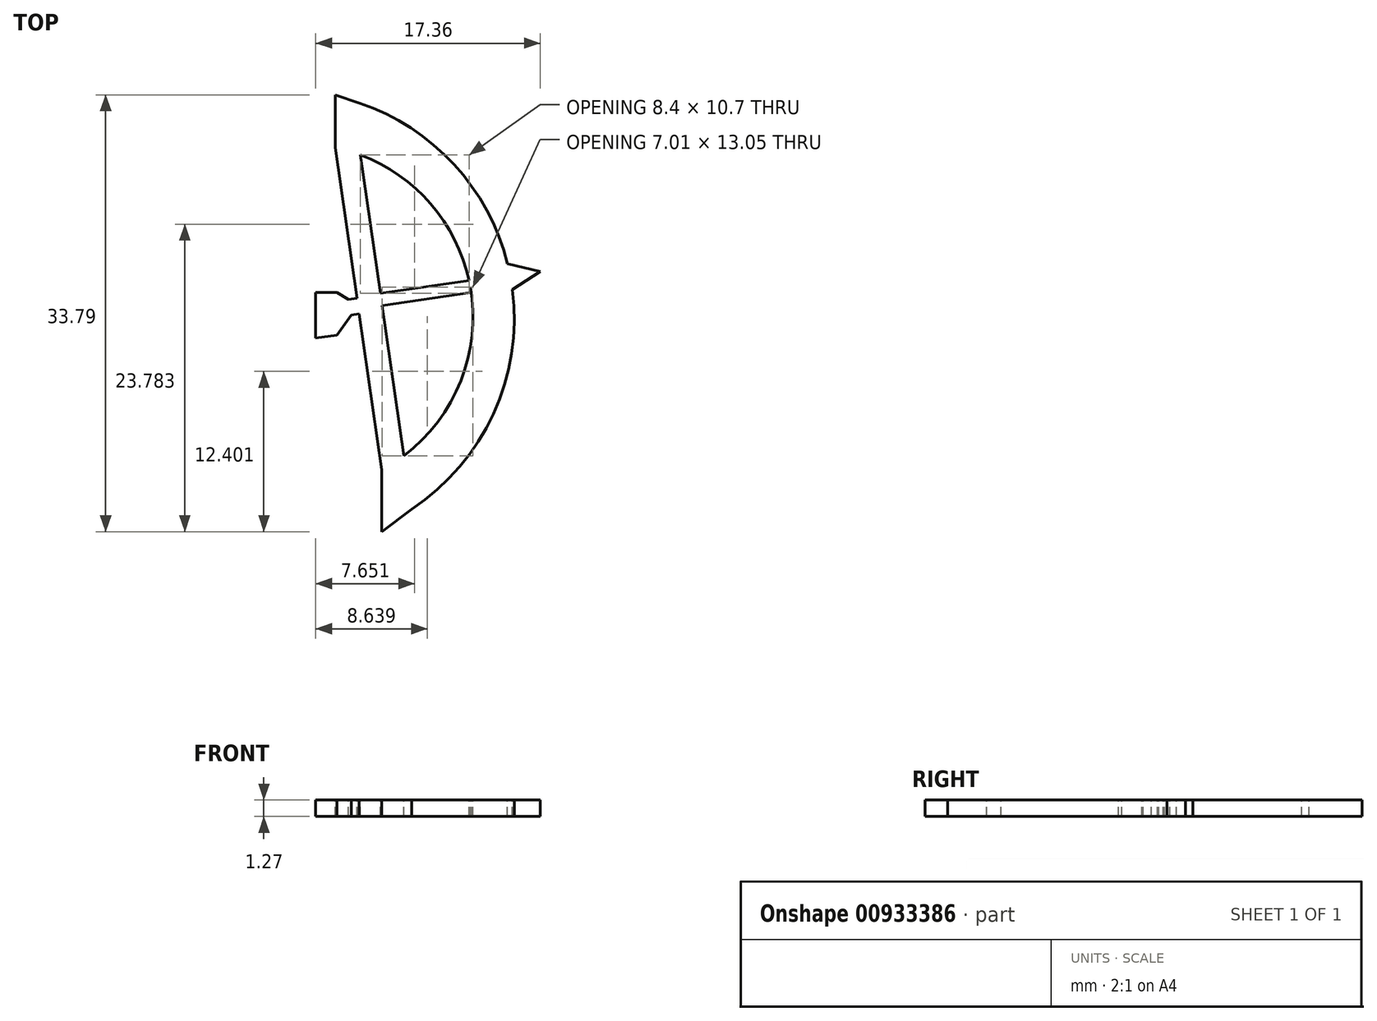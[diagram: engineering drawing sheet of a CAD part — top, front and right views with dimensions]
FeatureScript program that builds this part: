
annotation { "Feature Type Name" : "Feature", "Feature Type Description" : "" }
export const myFeature = defineFeature(function(context is Context, id is Id, definition is map)
    precondition{}
    {
        {
            var Q0;
            Q0=qCreatedBy(makeId("Top.planeOp"),FACE);
            var sketch = newSketch(context, id + "F0", { "sketchPlane" : qUnion([Q0])});
            skArc(sketch, "E0", {"start": v(-42.35, 8.79) * mm, "mid": v(-34.55, 25.75) * mm, "end": v(-46.38, 40.19) * mm});
            skArc(sketch, "E1", {"start": v(-44.65, 11.81) * mm, "mid": v(-37.73, 25.53) * mm, "end": v(-48.25, 36.73) * mm});
            skLineSegment(sketch, "E2", {"start": v(-46.38, 40.19) * mm, "end": v(-48.25, 36.73) * mm});
            skLineSegment(sketch, "E3", {"start": v(-44.65, 11.81) * mm, "end": v(-42.35, 8.79) * mm});
            skLineSegment(sketch, "E4", {"start": v(-46.38, 40.19) * mm, "end": v(-48.25, 40.82) * mm});
            skLineSegment(sketch, "E5", {"start": v(-48.25, 40.82) * mm, "end": v(-48.25, 36.73) * mm});
            skLineSegment(sketch, "E6", {"start": v(-42.35, 8.79) * mm, "end": v(-44.65, 7.03) * mm});
            skLineSegment(sketch, "E7", {"start": v(-44.65, 7.03) * mm, "end": v(-44.65, 11.81) * mm});
            skLineSegment(sketch, "E8", {"start": v(-48.25, 36.73) * mm, "end": v(-44.65, 11.81) * mm});
            skLineSegment(sketch, "E9", {"start": v(-46.38, 36.73) * mm, "end": v(-42.94, 12.9) * mm});
            skLineSegment(sketch, "E10", {"start": v(-37.73, 25.53) * mm, "end": v(-44.62, 24.53) * mm});
            skLineSegment(sketch, "E11", {"start": v(-44.62, 24.53) * mm, "end": v(-46.49, 24.53) * mm});
            skLineSegment(sketch, "E12", {"start": v(-46.49, 24.53) * mm, "end": v(-48.11, 25.55) * mm});
            skLineSegment(sketch, "E13", {"start": v(-48.11, 25.55) * mm, "end": v(-49.75, 25.55) * mm});
            skLineSegment(sketch, "E14", {"start": v(-49.75, 25.55) * mm, "end": v(-49.75, 23.61) * mm});
            skLineSegment(sketch, "E15", {"start": v(-49.75, 23.61) * mm, "end": v(-49.75, 22) * mm});
            skLineSegment(sketch, "E16", {"start": v(-49.75, 22) * mm, "end": v(-48.11, 22.23) * mm});
            skLineSegment(sketch, "E17", {"start": v(-48.11, 22.23) * mm, "end": v(-46.49, 24.53) * mm});
            skLineSegment(sketch, "E18", {"start": v(-47.01, 23.79) * mm, "end": v(-46.4, 23.88) * mm});
            skLineSegment(sketch, "E19", {"start": v(-46.4, 23.88) * mm, "end": v(-46.57, 25.1) * mm});
            skLineSegment(sketch, "E20", {"start": v(-46.57, 25.1) * mm, "end": v(-47.23, 25) * mm});
            skLineSegment(sketch, "E21", {"start": v(-34.92, 27.75) * mm, "end": v(-32.39, 27.17) * mm});
            skLineSegment(sketch, "E22", {"start": v(-32.39, 27.17) * mm, "end": v(-34.55, 25.75) * mm});
            skLineSegment(sketch, "E23", {"start": v(-44.55, 24.1) * mm, "end": v(-37.68, 25.1) * mm});
            skLineSegment(sketch, "E24", {"start": v(-37.68, 25.1) * mm, "end": v(-37.8, 25.95) * mm});
            skLineSegment(sketch, "E25", {"start": v(-37.8, 25.95) * mm, "end": v(-44.68, 24.96) * mm});
            skLineSegment(sketch, "E26", {"start": v(-44.75, 25.47) * mm, "end": v(-37.9, 26.46) * mm});
            skSolve(sketch);
        }
        {
            var Q0;
            {var subQ7=sQuery(id+"F0.wireOp",EDGE,"E2");Q0=makeQuery(id+"F0.imprint","IMPRINT",FACE,{"disambiguationData":[TD([[makeQuery(id+"F0.imprint","IMPRINT",EDGE,{"derivedFrom":subQ7}),1.0]])]});}
            var Q1;
            {var subQ7=sQuery(id+"F0.wireOp",EDGE,"E11");Q1=makeQuery(id+"F0.imprint","IMPRINT",FACE,{"disambiguationData":[TD([[makeQuery(id+"F0.imprint","IMPRINT",EDGE,{"derivedFrom":subQ7}),1.0]])]});}
            var Q2;
            {var subQ4=sQuery(id+"F0.wireOp",EDGE,"E11");Q2=makeQuery(id+"F0.imprint","IMPRINT",FACE,{"disambiguationData":[TD([[makeQuery(id+"F0.imprint","IMPRINT",EDGE,{"derivedFrom":subQ4}),-1.0]])]});}
            var Q3;
            {var subQ0=sQuery(id+"F0.wireOp",EDGE,"E13");Q3=makeQuery(id+"F0.imprint","IMPRINT",FACE,{"disambiguationData":[TD([[makeQuery(id+"F0.imprint","IMPRINT",EDGE,{"derivedFrom":subQ0}),1.0]])]});}
            var Q4;
            {var subQ2=sQuery(id+"F0.wireOp",EDGE,"E21");Q4=makeQuery(id+"F0.imprint","IMPRINT",FACE,{"disambiguationData":[TD([[makeQuery(id+"F0.imprint","IMPRINT",EDGE,{"derivedFrom":subQ2}),-1.0]])]});}
            var Q5;
            Q5=makeQuery(id+"F0.imprint","IMPRINT",FACE,{"disambiguationData":[TD([[makeQuery(id+"F0.imprint","IMPRINT",EDGE,{"derivedFrom":sQuery(id+"F0.wireOp",EDGE,"E3")}),-1.0]])]});
            var Q6;
            Q6=makeQuery(id+"F0.imprint","IMPRINT",FACE,{"disambiguationData":[TD([[makeQuery(id+"F0.imprint","IMPRINT",EDGE,{"derivedFrom":sQuery(id+"F0.wireOp",EDGE,"E2")}),-1.0]])]});
            var Q7;
            {var subQ0=sQuery(id+"F0.wireOp",EDGE,"E25");Q7=makeQuery(id+"F0.imprint","IMPRINT",FACE,{"disambiguationData":[TD([[makeQuery(id+"F0.imprint","IMPRINT",EDGE,{"derivedFrom":subQ0}),-1.0]])]});}
            var Q8;
            {var subQ3=sQuery(id+"F0.wireOp",EDGE,"E25");Q8=makeQuery(id+"F0.imprint","IMPRINT",FACE,{"disambiguationData":[TD([[makeQuery(id+"F0.imprint","IMPRINT",EDGE,{"derivedFrom":subQ3}),1.0]])]});}
            var Q9;
            {var subQ3=sQuery(id+"F0.wireOp",EDGE,"E20");Q9=makeQuery(id+"F0.imprint","IMPRINT",FACE,{"disambiguationData":[TD([[makeQuery(id+"F0.imprint","IMPRINT",EDGE,{"derivedFrom":subQ3}),1.0]])]});}
            var Q10;
            {var subQ0=sQuery(id+"F0.wireOp",EDGE,"E18");Q10=makeQuery(id+"F0.imprint","IMPRINT",FACE,{"disambiguationData":[TD([[makeQuery(id+"F0.imprint","IMPRINT",EDGE,{"derivedFrom":subQ0}),1.0]])]});}
            extrude(context, id + "F1", {"entities" : qUnion([Q0, Q1, Q2, Q3, Q4, Q5, Q6, Q7, Q8, Q9, Q10]), "oppositeDirection" : true, "depth" : 1.27 * mm, "offsetDistance" : 25.4 * mm});
        }
    });
